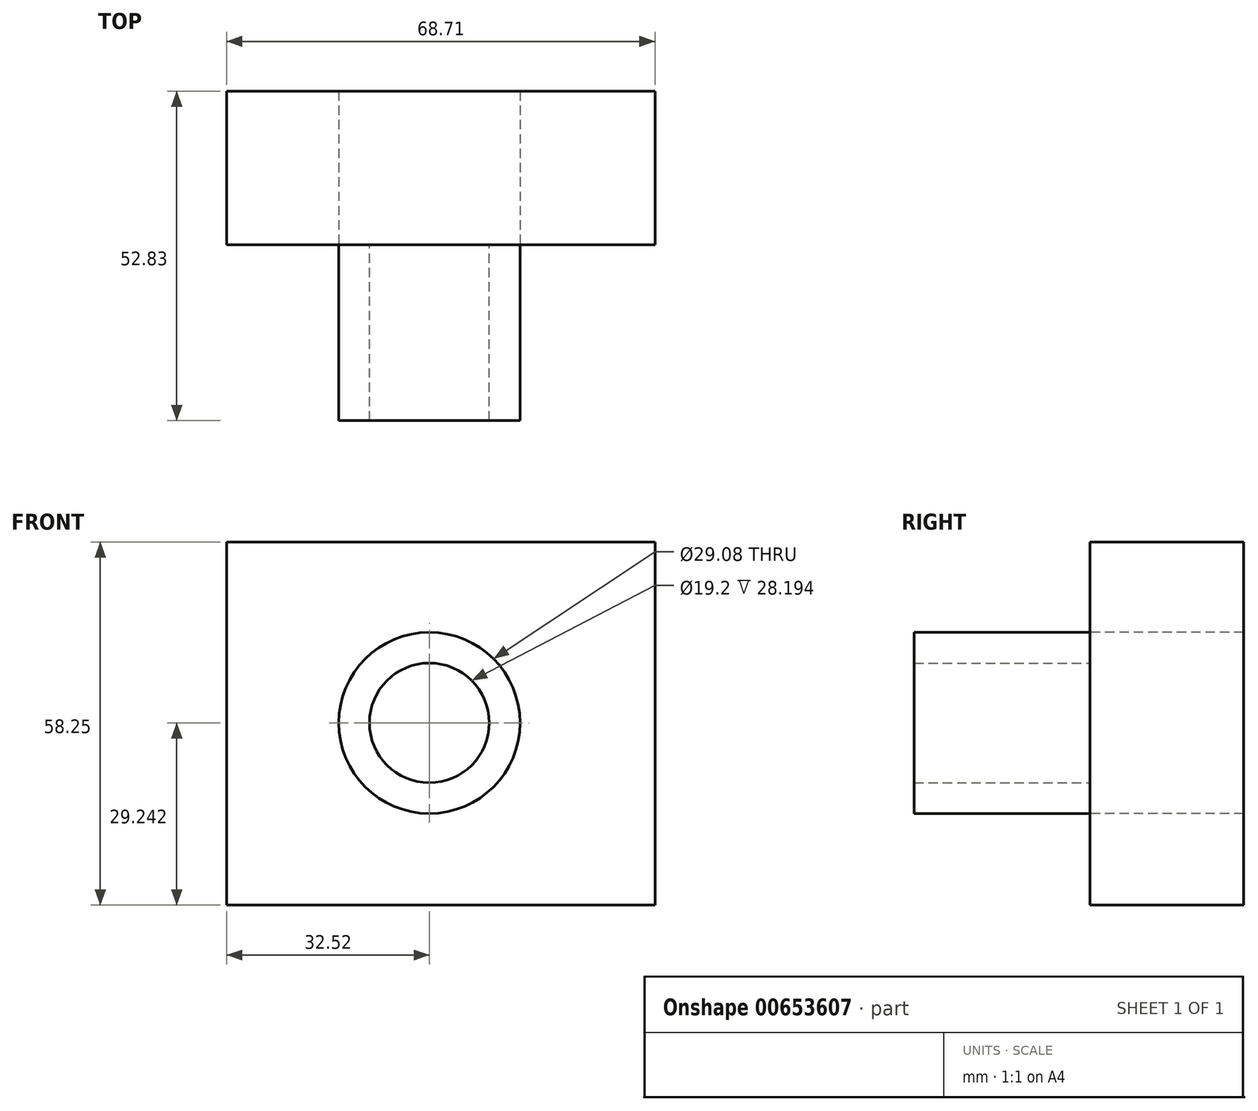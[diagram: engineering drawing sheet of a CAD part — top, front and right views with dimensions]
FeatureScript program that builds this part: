
annotation { "Feature Type Name" : "Feature", "Feature Type Description" : "" }
export const myFeature = defineFeature(function(context is Context, id is Id, definition is map)
    precondition{}
    {
        {
            var Q0;
            Q0=qCreatedBy(makeId("Front.planeOp"),FACE);
            var sketch = newSketch(context, id + "F0", { "sketchPlane" : qUnion([Q0])});
            skLineSegment(sketch, "E0", {"start": v(-32.52, 40.46) * mm, "end": v(36.19, 40.46) * mm});
            skLineSegment(sketch, "E1", {"start": v(36.19, 40.46) * mm, "end": v(36.19, -17.8) * mm});
            skLineSegment(sketch, "E2", {"start": v(36.19, -17.8) * mm, "end": v(-32.52, -17.8) * mm});
            skLineSegment(sketch, "E3", {"start": v(-32.52, 40.46) * mm, "end": v(-32.52, -17.8) * mm});
            skSolve(sketch);
        }
        {
            var Q0;
            Q0=makeQuery(id+"F0.imprint","IMPRINT",FACE,{"disambiguationData":[TD([[makeQuery(id+"F0.imprint","IMPRINT",EDGE,{"derivedFrom":sQuery(id+"F0.wireOp",EDGE,"E0")}),-1.0]])]});
            var sketch = newSketch(context, id + "F1", { "sketchPlane" : qUnion([Q0])});
            skCircle(sketch, "E4", {"center": v(0, 11.45) * mm, "radius": 14.54 * mm});
            skCircle(sketch, "E5", {"center": v(0, 11.45) * mm, "radius": 9.6 * mm});
            skSolve(sketch);
        }
        {
            var Q0;
            Q0=makeQuery(id+"F1.imprint","IMPRINT",FACE,{"disambiguationData":[TD([[makeQuery(id+"F1.imprint","IMPRINT",EDGE,{"derivedFrom":sQuery(id+"F1.wireOp",EDGE,"E4")}),-1.0]])]});
            extrude(context, id + "F2", {"entities" : qUnion([Q0]), "oppositeDirection" : true, "depth" : 24.64 * mm, "offsetDistance" : 25.4 * mm});
        }
        {
            var Q0;
            Q0=makeQuery(id+"F1.imprint","IMPRINT",FACE,{"disambiguationData":[TD([[makeQuery(id+"F1.imprint","IMPRINT",EDGE,{"derivedFrom":sQuery(id+"F1.wireOp",EDGE,"E4")}),1.0]])]});
            extrude(context, id + "F3", {"entities" : qUnion([Q0]), "depth" : 28.2 * mm, "offsetDistance" : 25.4 * mm});
        }
    });
